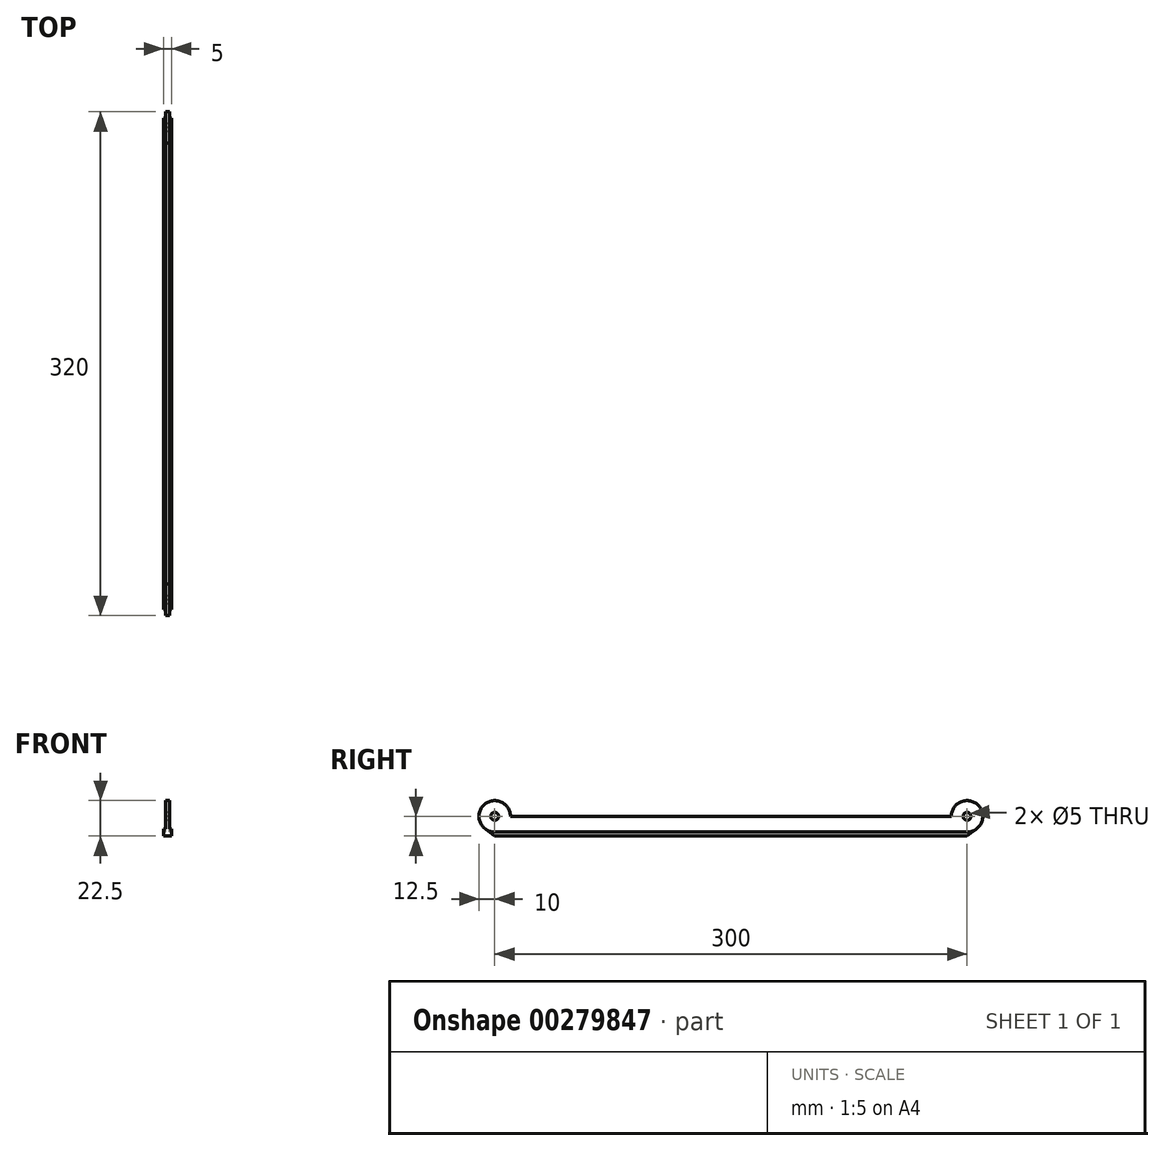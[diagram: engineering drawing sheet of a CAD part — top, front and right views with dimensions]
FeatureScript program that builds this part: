
annotation { "Feature Type Name" : "Feature", "Feature Type Description" : "" }
export const myFeature = defineFeature(function(context is Context, id is Id, definition is map)
    precondition{}
    {
        {
            var Q0;
            Q0=qCreatedBy(makeId("Right.planeOp"),FACE);
            var sketch = newSketch(context, id + "F0", { "sketchPlane" : qUnion([Q0])});
            skCircle(sketch, "E0", {"center": v(-150, 12.5) * mm, "radius": 10 * mm});
            skCircle(sketch, "E1", {"center": v(150, 12.5) * mm, "radius": 10 * mm});
            skCircle(sketch, "E2", {"center": v(-150, 12.5) * mm, "radius": 2.5 * mm});
            skCircle(sketch, "E3", {"center": v(150, 12.5) * mm, "radius": 2.5 * mm});
            skLineSegment(sketch, "E4", {"start": v(-150, 2.5) * mm, "end": v(150, 2.5) * mm});
            skLineSegment(sketch, "E5", {"start": v(-150, 0) * mm, "end": v(150, 0) * mm});
            skLineSegment(sketch, "E6", {"start": v(-140, 12.5) * mm, "end": v(140, 12.5) * mm});
            skLineSegment(sketch, "E7", {"start": v(-150, 0) * mm, "end": v(-156, 4.5) * mm});
            skLineSegment(sketch, "E8", {"start": v(150, 0) * mm, "end": v(156, 4.5) * mm});
            skLineSegment(sketch, "E9", {"start": v(-150, 12.5) * mm, "end": v(-140, 12.5) * mm, "construction": true});
            skLineSegment(sketch, "E10", {"start": v(140, 12.5) * mm, "end": v(150, 12.5) * mm, "construction": true});
            skLineSegment(sketch, "E11", {"start": v(-150, 12.5) * mm, "end": v(-150, 2.5) * mm, "construction": true});
            skLineSegment(sketch, "E12", {"start": v(150, 12.5) * mm, "end": v(150, 2.5) * mm, "construction": true});
            skLineSegment(sketch, "E13", {"start": v(-150, 2.5) * mm, "end": v(-150, 0) * mm, "construction": true});
            skLineSegment(sketch, "E14", {"start": v(150, 2.5) * mm, "end": v(150, 0) * mm, "construction": true});
            skSolve(sketch);
        }
        {
            var Q0;
            {var subQ0=sQuery(id+"F0.wireOp",EDGE,"E4");Q0=makeQuery(id+"F0.imprint","IMPRINT",FACE,{"disambiguationData":[TD([[makeQuery(id+"F0.imprint","IMPRINT",EDGE,{"derivedFrom":subQ0}),-1.0]])]});}
            extrude(context, id + "F1", {"entities" : qUnion([Q0]), "endBound" : BoundingType.SYMMETRIC, "depth" : 5 * mm});
        }
        {
            var Q0;
            {var subQ0=sQuery(id+"F0.wireOp",EDGE,"E4");Q0=makeQuery(id+"F0.imprint","IMPRINT",FACE,{"disambiguationData":[TD([[makeQuery(id+"F0.imprint","IMPRINT",EDGE,{"derivedFrom":subQ0}),1.0]])]});}
            var Q1;
            Q1=makeQuery(id+"F0.imprint","IMPRINT",FACE,{"disambiguationData":[TD([[makeQuery(id+"F0.imprint","IMPRINT",EDGE,{"derivedFrom":sQuery(id+"F0.wireOp",EDGE,"E2")}),-1.0]])]});
            var Q2;
            Q2=makeQuery(id+"F0.imprint","IMPRINT",FACE,{"disambiguationData":[TD([[makeQuery(id+"F0.imprint","IMPRINT",EDGE,{"derivedFrom":sQuery(id+"F0.wireOp",EDGE,"E3")}),-1.0]])]});
            extrude(context, id + "F2", {"entities" : qUnion([Q0, Q1, Q2]), "operationType" : NewBodyOperationType.ADD, "endBound" : BoundingType.SYMMETRIC, "depth" : 2.5 * mm});
        }
    });
